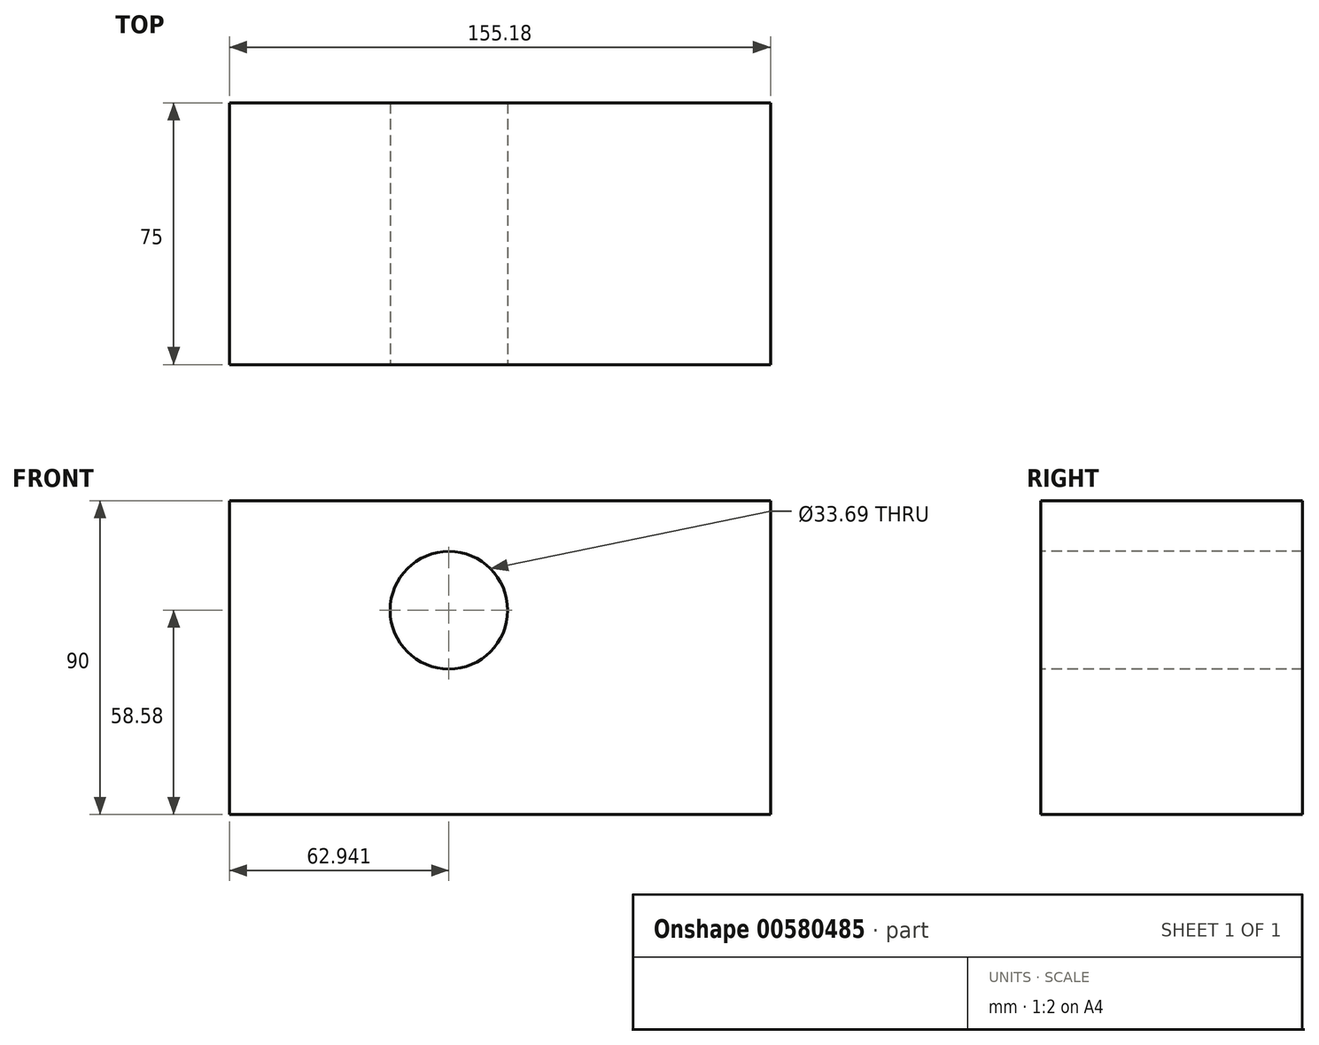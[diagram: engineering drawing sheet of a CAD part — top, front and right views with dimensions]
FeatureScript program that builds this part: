
annotation { "Feature Type Name" : "Feature", "Feature Type Description" : "" }
export const myFeature = defineFeature(function(context is Context, id is Id, definition is map)
    precondition{}
    {
        {
            var Q0;
            Q0=qCreatedBy(makeId("Front.planeOp"),FACE);
            var sketch = newSketch(context, id + "F0", { "sketchPlane" : qUnion([Q0])});
            skLineSegment(sketch, "E0.bottom", {"start": v(-49.87, 31.42) * mm, "end": v(105.3, 31.42) * mm});
            skLineSegment(sketch, "E0.top", {"start": v(-49.87, -58.58) * mm, "end": v(105.3, -58.58) * mm});
            skLineSegment(sketch, "E0.left", {"start": v(-49.87, 31.42) * mm, "end": v(-49.87, -58.58) * mm});
            skLineSegment(sketch, "E0.right", {"start": v(105.3, 31.42) * mm, "end": v(105.3, -58.58) * mm});
            skSolve(sketch);
        }
        {
            var Q0;
            Q0 = qSketchRegion(id + "F0", true);
            extrude(context, id + "F1", {"entities" : qUnion([Q0]), "depth" : 25 * mm, "offsetDistance" : 25 * mm});
        }
        {
            var Q0;
            Q0=makeQuery(id+"F1.opExtrude","CAP_FACE",FACE,{"disambiguationData":[OSD([sQuery(id+"F0.wireOp",EDGE,"E0.bottom"),sQuery(id+"F0.wireOp",EDGE,"E0.top"),sQuery(id+"F0.wireOp",EDGE,"E0.left"),sQuery(id+"F0.wireOp",EDGE,"E0.right")])],"isStart":false});
            var sketch = newSketch(context, id + "F2", { "sketchPlane" : qUnion([Q0])});
            skCircle(sketch, "E1", {"center": v(13.07, 0) * mm, "radius": 16.85 * mm});
            skSolve(sketch);
        }
        {
            var Q0;
            Q0 = qSketchRegion(id + "F2", true);
            extrude(context, id + "F3", {"entities" : qUnion([Q0]), "operationType" : NewBodyOperationType.REMOVE, "endBound" : BoundingType.THROUGH_ALL, "oppositeDirection" : true, "depth" : 25 * mm, "offsetDistance" : 25 * mm});
        }
        {
            var Q0;
            Q0=makeQuery(id+"F1.opExtrude","CAP_FACE",FACE,{"disambiguationData":[OSD([sQuery(id+"F0.wireOp",EDGE,"E0.bottom"),sQuery(id+"F0.wireOp",EDGE,"E0.top"),sQuery(id+"F0.wireOp",EDGE,"E0.left"),sQuery(id+"F0.wireOp",EDGE,"E0.right")])],"isStart":false});
            extrude(context, id + "F4", {"entities" : qUnion([Q0]), "operationType" : NewBodyOperationType.ADD, "depth" : 50 * mm, "offsetDistance" : 25 * mm});
        }
    });
